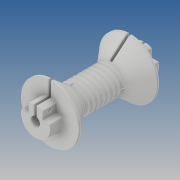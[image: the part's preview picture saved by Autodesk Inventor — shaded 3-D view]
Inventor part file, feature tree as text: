
AUTODESK INVENTOR PART (.ipt)
format: ipt  version: 2019 (Build 230136000, 136)  size: 308,736 bytes
history: native  units: mm
features: sketch x4, other x3, projected_geometry x3, extrude x2, hole x1, mirror x1, fillet x1
ambient origin geometry x8: Origin, YZ Plane, XZ Plane, XY Plane, X Axis, Y Axis, Z Axis, Center Point
bodies: Solide1 (feature_tree)
feature tree (15):
  other  "Révolution1"
  extrude  "Extrusion1"  Depth=6.25mm
  extrude  "Extrusion2"  Depth=20.0mm
  hole  "Perçage1"  [1 undecoded]
  mirror  "Symétrie1"
  other  "Hélicoïde1"
  fillet  "Congé1"  Radius=24.43461mm
  sketch  "Esquisse1"
  sketch  "Esquisse2"
  projected_geometry  "Boucle projetée1"
  sketch  "Esquisse3"
  projected_geometry  "Boucle projetée2"
  projected_geometry  "Boucle projetée3"
  sketch  "Esquisse5"
  other  "Projeter les arêtes coupées1"
note: 1 required parameter value undecoded (feature->parameter linkage not recoverable at this tier; creation-order binding heuristic only, values carry confidence <= 0.55)
